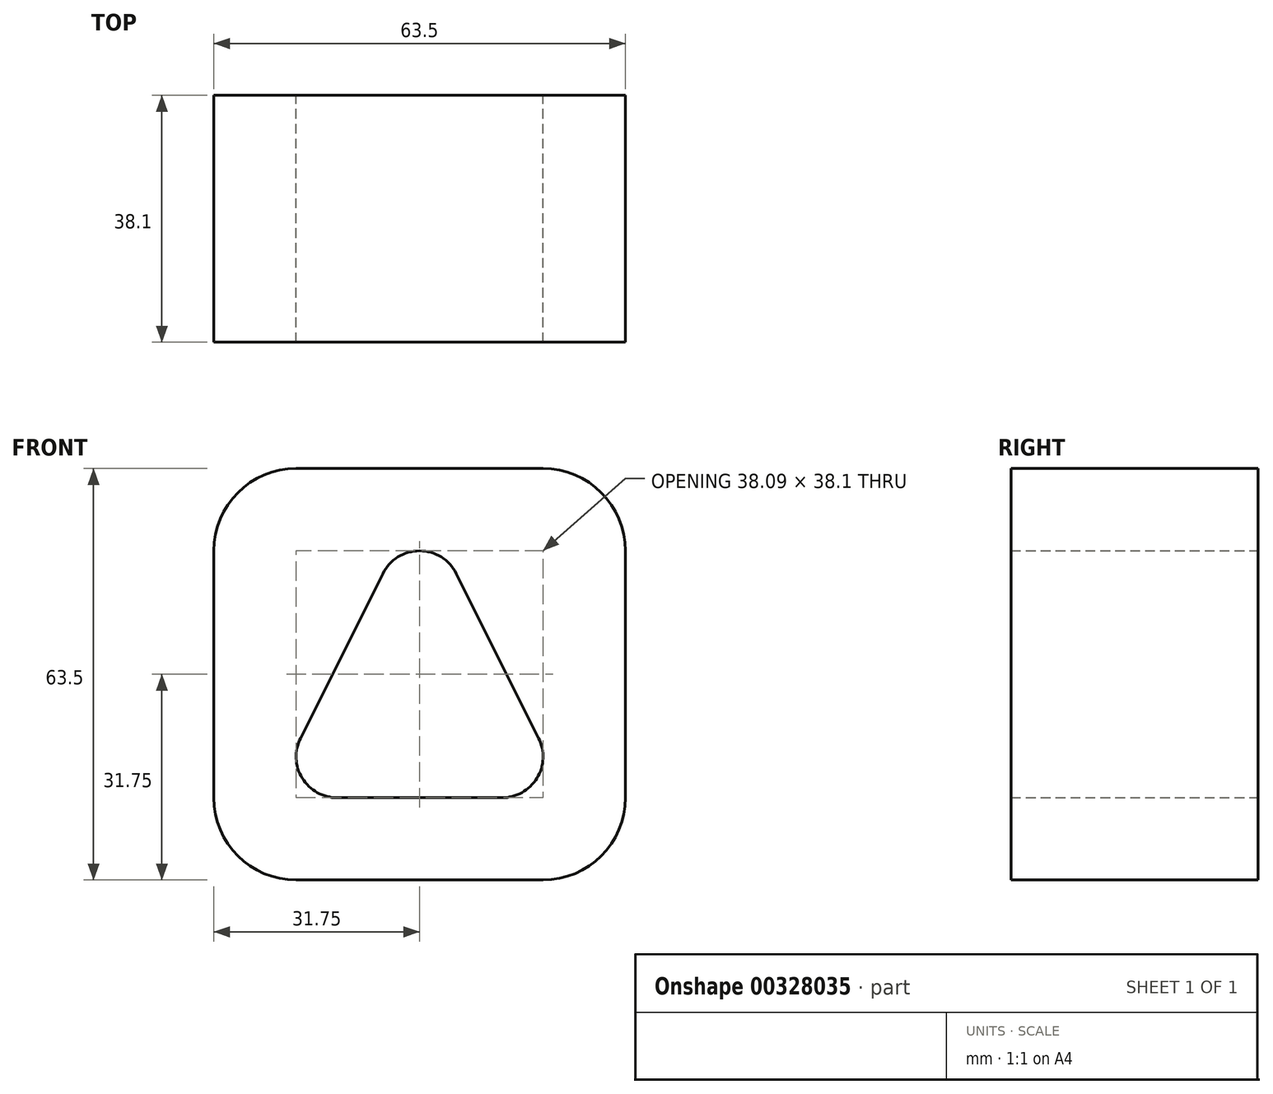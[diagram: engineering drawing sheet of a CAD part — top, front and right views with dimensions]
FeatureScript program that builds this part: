
annotation { "Feature Type Name" : "Feature", "Feature Type Description" : "" }
export const myFeature = defineFeature(function(context is Context, id is Id, definition is map)
    precondition{}
    {
        {
            var Q0;
            Q0=qCreatedBy(makeId("Front.planeOp"),FACE);
            var sketch = newSketch(context, id + "F0", { "sketchPlane" : qUnion([Q0])});
            skLineSegment(sketch, "E0.bottom", {"start": v(0, 0) * mm, "end": v(63.5, 0) * mm});
            skLineSegment(sketch, "E0.top", {"start": v(0, 63.5) * mm, "end": v(63.5, 63.5) * mm});
            skLineSegment(sketch, "E0.left", {"start": v(0, 0) * mm, "end": v(0, 63.5) * mm});
            skLineSegment(sketch, "E0.right", {"start": v(63.5, 0) * mm, "end": v(63.5, 63.5) * mm});
            skArc(sketch, "E1", {"start": v(13.37, 21.89) * mm, "mid": v(13.65, 15.71) * mm, "end": v(19.05, 12.7) * mm});
            skArc(sketch, "E2", {"start": v(37.43, 47.29) * mm, "mid": v(31.75, 50.8) * mm, "end": v(26.07, 47.29) * mm});
            skArc(sketch, "E3", {"start": v(44.45, 12.7) * mm, "mid": v(49.85, 15.71) * mm, "end": v(50.13, 21.89) * mm});
            skLineSegment(sketch, "E4", {"start": v(37.43, 47.29) * mm, "end": v(50.13, 21.89) * mm});
            skLineSegment(sketch, "E5", {"start": v(26.07, 47.29) * mm, "end": v(13.37, 21.89) * mm});
            skLineSegment(sketch, "E6", {"start": v(19.05, 12.7) * mm, "end": v(44.45, 12.7) * mm});
            skSolve(sketch);
        }
        {
            var Q0;
            Q0=makeQuery(id+"F0.imprint","IMPRINT",FACE,{"disambiguationData":[TD([[makeQuery(id+"F0.imprint","IMPRINT",EDGE,{"derivedFrom":sQuery(id+"F0.wireOp",EDGE,"E0.bottom")}),1.0]])]});
            extrude(context, id + "F1", {"entities" : qUnion([Q0]), "depth" : 38.1 * mm, "symmetric" : true});
        }
        {
            var Q0;
            Q0=makeQuery(id+"F1.opExtrude","SWEPT_EDGE",EDGE,{"disambiguationData":[OSD([sQuery(id+"F0.wireOp",EDGE,"E0.bottom"),sQuery(id+"F0.wireOp",EDGE,"E0.right")])]});
            var Q1;
            Q1=makeQuery(id+"F1.opExtrude","SWEPT_EDGE",EDGE,{"disambiguationData":[OSD([sQuery(id+"F0.wireOp",EDGE,"E0.top"),sQuery(id+"F0.wireOp",EDGE,"E0.right")])]});
            var Q2;
            Q2=makeQuery(id+"F1.opExtrude","SWEPT_EDGE",EDGE,{"disambiguationData":[OSD([sQuery(id+"F0.wireOp",EDGE,"E0.bottom"),sQuery(id+"F0.wireOp",EDGE,"E0.left")])]});
            var Q3;
            Q3=makeQuery(id+"F1.opExtrude","SWEPT_EDGE",EDGE,{"disambiguationData":[OSD([sQuery(id+"F0.wireOp",EDGE,"E0.top"),sQuery(id+"F0.wireOp",EDGE,"E0.left")])]});
            fillet(context, id + "F2", {"entities" : qUnion([Q0, Q1, Q2, Q3]), "radius" : 12.7 * mm, "tangentPropagation" : true, "allowEdgeOverflow" : false});
        }
    });
